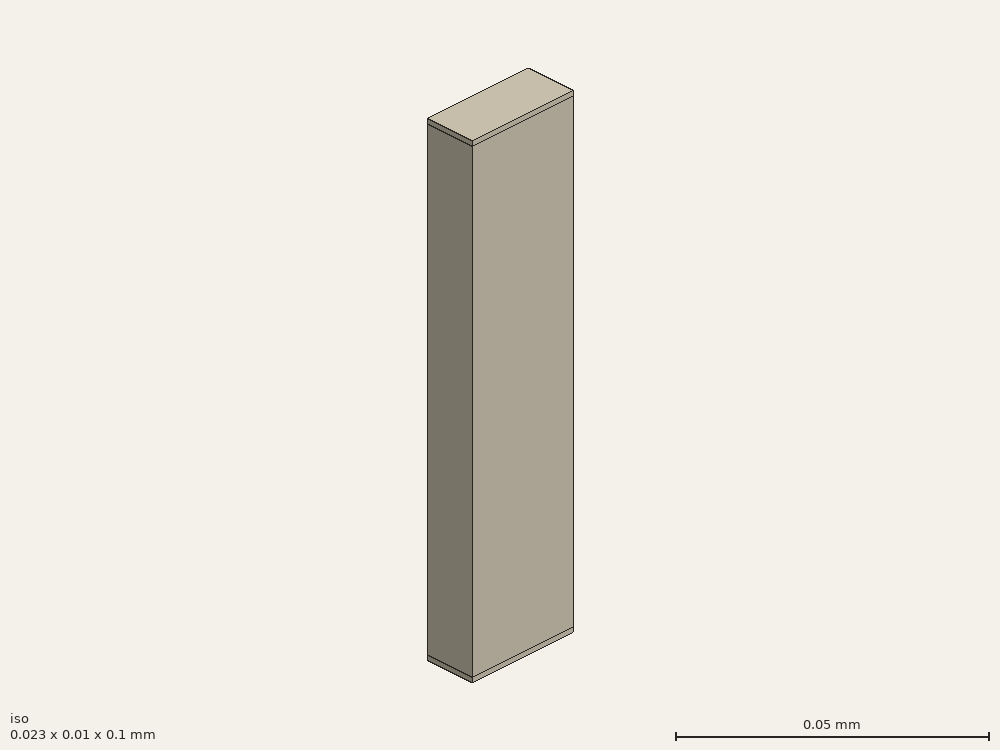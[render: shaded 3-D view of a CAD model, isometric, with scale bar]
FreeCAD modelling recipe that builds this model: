
FCSTD DOCUMENT  (FreeCAD 0.21R33694 (Git))
Label: straight
License: All rights reserved
LicenseURL: http://en.wikipedia.org/wiki/All_rights_reserved
objects: Part::Part2DObjectPython×13, App::FeaturePython×12, Part::Extrusion×1, Part::FeaturePython×1
note: 15 computed .brp shape members not serialized (recipe doc carries the construction recipe); baked Part::Feature solids carry a one-line shape summary decoded from their .brp

FEATURE [Part::Part2DObjectPython] Rectangle001  label="_Pport1"  # Draft 2D object (typed FeaturePython)
  Area = 0.000232258
  ChamferSize = 0
  Columns = 1
  FilletRadius = 0
  Height = 0.01016
  Length = 0.02286
  MakeFace = true
  Placement = pos=(-0.01143,-0.00508,0.1) rot=(0,0,1;0rad)
  Rows = 1
FEATURE [Part::Part2DObjectPython] Line  label="_Pv1"  # Draft 2D object (typed FeaturePython)
  Area = 0
  ChamferSize = 0
  Closed = false
  End = (-1.8e-15,0.00508,0.1)
  FilletRadius = 0
  Length = 0.01016
  MakeFace = true
  Placement = pos=(0,-0.00508,0.1) rot=(0,0,1;0rad)
  Points = (2) [(0,0,0),(-1.77605e-15,0.01016,0)]
  Start = (0,-0.00508,0.1)
  Subdivisions = 0
FEATURE [Part::Part2DObjectPython] Rectangle002  label="_Pport2"  # Draft 2D object (typed FeaturePython)
  Area = 0.000232258
  ChamferSize = 0
  Columns = 1
  FilletRadius = 0
  Height = 0.01016
  Length = 0.02286
  MakeFace = true
  Placement = pos=(-0.01143,-0.00508,0) rot=(0,0,1;0rad)
  Rows = 1
FEATURE [Part::Part2DObjectPython] Line001  label="_Pv2"  # Draft 2D object (typed FeaturePython)
  Area = 0
  ChamferSize = 0
  Closed = false
  End = (0,0.00508,0)
  FilletRadius = 0
  Length = 0.01016
  MakeFace = true
  Placement = pos=(0,-0.00508,0) rot=(0,0,1;0rad)
  Points = (2) [(0,0,0),(3.1106e-19,0.01016,0)]
  Start = (0,-0.00508,0)
  Subdivisions = 0
FEATURE [App::FeaturePython] Text  label="_Sinput(PV){port1}"  # WARN: FeaturePython — macro-defined, semantics opaque (R4)
  Placement = pos=(0.0413747,-0.017509,0) rot=(0,0,1;0rad)
  Text = .
FEATURE [App::FeaturePython] Text001  label="_Soutput(PV){port2}"  # WARN: FeaturePython — macro-defined, semantics opaque (R4)
  Placement = pos=(0.0413747,-0.017509,0) rot=(0,0,1;0rad)
  Text = .
FEATURE [App::FeaturePython] Text002  label="_Linput(1,voltage){v1}"  # WARN: FeaturePython — macro-defined, semantics opaque (R4)
  Placement = pos=(0.0413747,-0.017509,0) rot=(0,0,1;0rad)
  Text = .
FEATURE [App::FeaturePython] Text003  label="_Loutput(2,voltage){v2}"  # WARN: FeaturePython — macro-defined, semantics opaque (R4)
  Placement = pos=(0.0413747,-0.017509,0) rot=(0,0,1;0rad)
  Text = .
FEATURE [App::FeaturePython] Text004  label="_B1(PEC){1}"  # WARN: FeaturePython — macro-defined, semantics opaque (R4)
  Placement = pos=(0.0413747,-0.017509,0) rot=(0,0,1;0rad)
  Text = .
FEATURE [Part::Part2DObjectPython] Rectangle007  # Draft 2D object (typed FeaturePython)
  Area = 0.000232258
  ChamferSize = 0
  Columns = 1
  FilletRadius = 0
  Height = 0.01016
  Length = 0.02286
  MakeFace = true
  Placement = pos=(-0.01143,-0.00508,0.1) rot=(0,0,1;0rad)
  Rows = 1
FEATURE [Part::Extrusion] Extrude001  label="waveguide"
  Base = -> Rectangle007
  Dir = (0,0,1)
  DirMode = 2
  FaceMakerClass = Part::FaceMakerBullseye
  LengthFwd = -0.1
  LengthRev = 0
  Solid = false
  Symmetric = false
FEATURE [Part::Part2DObjectPython] Rectangle  label="_P1"  # Draft 2D object (typed FeaturePython)
  Area = 2.286e-05
  ChamferSize = 0
  Columns = 1
  FilletRadius = 0
  Height = 0.001
  Length = 0.02286
  MakeFace = true
  Placement = pos=(-0.01143,-0.00508,0.099) rot=(1,0,0;1.5708rad)
  Rows = 1
FEATURE [Part::Part2DObjectPython] Rectangle008  label="_P2"  # Draft 2D object (typed FeaturePython)
  Area = 2.286e-05
  ChamferSize = 0
  Columns = 1
  FilletRadius = 0
  Height = 0.001
  Length = 0.02286
  MakeFace = true
  Placement = pos=(-0.01143,-0.00508,0) rot=(1,0,0;1.5708rad)
  Rows = 1
FEATURE [Part::Part2DObjectPython] Rectangle009  label="_P3"  # Draft 2D object (typed FeaturePython)
  Area = 1.016e-05
  ChamferSize = 0
  Columns = 1
  FilletRadius = 0
  Height = 0.001
  Length = 0.01016
  MakeFace = true
  Placement = pos=(0.01143,-0.00508,0.099) rot=(0.57735,0.57735,0.57735;2.0944rad)
  Rows = 1
FEATURE [Part::Part2DObjectPython] Rectangle010  label="_P4"  # Draft 2D object (typed FeaturePython)
  Area = 1.016e-05
  ChamferSize = 0
  Columns = 1
  FilletRadius = 0
  Height = 0.001
  Length = 0.01016
  MakeFace = true
  Placement = pos=(0.01143,-0.00508,0) rot=(0.57735,0.57735,0.57735;2.0944rad)
  Rows = 1
FEATURE [Part::Part2DObjectPython] Rectangle011  label="_P5"  # Draft 2D object (typed FeaturePython)
  Area = 2.286e-05
  ChamferSize = 0
  Columns = 1
  FilletRadius = 0
  Height = 0.001
  Length = 0.02286
  MakeFace = true
  Placement = pos=(0.01143,0.00508,0.099) rot=(0,0.707107,0.707107;3.14159rad)
  Rows = 1
FEATURE [Part::Part2DObjectPython] Rectangle012  label="_P6"  # Draft 2D object (typed FeaturePython)
  Area = 2.286e-05
  ChamferSize = 0
  Columns = 1
  FilletRadius = 0
  Height = 0.001
  Length = 0.02286
  MakeFace = true
  Placement = pos=(0.01143,0.00508,0) rot=(0,0.707107,0.707107;3.14159rad)
  Rows = 1
FEATURE [Part::Part2DObjectPython] Rectangle013  label="_P7"  # Draft 2D object (typed FeaturePython)
  Area = 1.016e-05
  ChamferSize = 0
  Columns = 1
  FilletRadius = 0
  Height = 0.001
  Length = 0.01016
  MakeFace = true
  Placement = pos=(-0.01143,-0.00508,0.099) rot=(0.57735,0.57735,0.57735;2.0944rad)
  Rows = 1
FEATURE [Part::Part2DObjectPython] Rectangle014  label="_P8"  # Draft 2D object (typed FeaturePython)
  Area = 1.016e-05
  ChamferSize = 0
  Columns = 1
  FilletRadius = 0
  Height = 0.001
  Length = 0.01016
  MakeFace = true
  Placement = pos=(-0.01143,-0.00508,0) rot=(0.57735,0.57735,0.57735;2.0944rad)
  Rows = 1
FEATURE [App::FeaturePython] Text005  label="_B2(PEC){2}"  # WARN: FeaturePython — macro-defined, semantics opaque (R4)
  Placement = pos=(0.0413747,-0.017509,0) rot=(0,0,1;0rad)
  Text = .
FEATURE [App::FeaturePython] Text006  label="_B3(PEC){3}"  # WARN: FeaturePython — macro-defined, semantics opaque (R4)
  Placement = pos=(0.0413747,-0.017509,0) rot=(0,0,1;0rad)
  Text = .
FEATURE [App::FeaturePython] Text007  label="_B4(PEC){4}"  # WARN: FeaturePython — macro-defined, semantics opaque (R4)
  Placement = pos=(0.0413747,-0.017509,0) rot=(0,0,1;0rad)
  Text = .
FEATURE [App::FeaturePython] Text008  label="_B5(PEC){5}"  # WARN: FeaturePython — macro-defined, semantics opaque (R4)
  Placement = pos=(0.0413747,-0.017509,0) rot=(0,0,1;0rad)
  Text = .
FEATURE [App::FeaturePython] Text009  label="_B6(PEC){6}"  # WARN: FeaturePython — macro-defined, semantics opaque (R4)
  Placement = pos=(0.0413747,-0.017509,0) rot=(0,0,1;0rad)
  Text = .
FEATURE [App::FeaturePython] Text010  label="_B7(PEC){7}"  # WARN: FeaturePython — macro-defined, semantics opaque (R4)
  Placement = pos=(0.0413747,-0.017509,0) rot=(0,0,1;0rad)
  Text = .
FEATURE [App::FeaturePython] Text011  label="_B8(PEC){8}"  # WARN: FeaturePython — macro-defined, semantics opaque (R4)
  Placement = pos=(0.0413747,-0.017509,0) rot=(0,0,1;0rad)
  Text = .
FEATURE [Part::FeaturePython] BooleanFragments  # WARN: FeaturePython — macro-defined, semantics opaque (R4)
  Mode = 0
  Objects = -> [Extrude001,Rectangle,Rectangle008,Rectangle009,Rectangle010,Rectangle011,Rectangle012,Rectangle013,Rectangle014]
  Tolerance = 0
